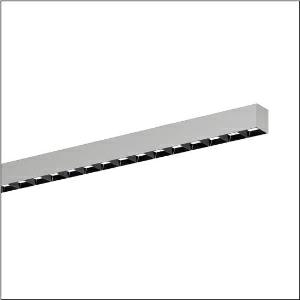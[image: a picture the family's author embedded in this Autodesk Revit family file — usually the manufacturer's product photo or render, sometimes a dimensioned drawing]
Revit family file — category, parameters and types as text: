
# Revit family: silica_r__21_51mx21dc3asb_b009
name_source: partatom
category: Lighting Fixtures
units: mm (PartAtom-declared; Revit-internal decimal feet)

## family parameters
Cut with Voids When Loaded = No
Host = Face
Light Source = No
Part Type = Normal
Room Calculation Point = No
Round Connector Dimension = Use Diameter
Shared = No

## types (1)
- --- (1 x LED, 10800 lm, 69.3 W, 3000K)
    Apparent Load = 69 VA
    CIE Flux Codes = 87 99 100 100 100
    Color Rendering = 80
    Color Temperature = 3000K
    Default Elevation = 1800 mm
    Description = Silica® 21, office luminaire, primary light control with darklight reflector, of PMMA, black, CAT 2 (L<= 3000cd/m²), light emission: direct distribution, primary light characteristic: symmetric, installation type: surface-mounted, LED, rated luminous flux: 10.800lm, luminous efficacy: 156lm/W, light colour: 830, colour temperature: 3000K, with terminal, 3+2-pole, max. 2.5mm², mains connection: 220..240V, AC, 50/60Hz, luminaire housing, of aluminium, metallic grey (RAL 9006), length: 3.004mm, width: 53mm, height: 53mm, protection rating (complete): IP20, insulation class (complete): insulation class I (protective earthing), certification: CE, permissible operating ambient temperature: 0..+35°C, standard: EN 50419, packaging unit: 1 piece
    Height = 0 mm  [stored 0 ft]
    Lamp = 1 x LED
    Lamp Light Flux = 10800 lm
    Lamp Power = 69.3 W
    Lamp count = 1
    Length = 3004 mm
    Luminous efficacy = 156 lm/W
    Manufacturer = Siteco
    ModVariant = No
    Model = 51MX21DC3ASB
    Mounting Place = Ceiling
    Mounting Type = Recessed
    Number of Poles = 1
    OnlyDefault = Yes
    Power Factor = 1
    Product Name = Silica® 21
    Product group = office luminaire | ceiling recessed
    ProductGroupID = 400
    Protection Class = Protection class I
    Protection Degree = IP 20
    RLX_Detail_Level = 1
    RLX_Emergency_Light_Flux = 0 lm
    RLX_Emergency_Type = 0
    RLX_Emergency_Type_DB = No
    RlxData = <blob elided: 63573 chars, md5=67ed1f3a>
    Socket = socket
    Standby Power = 0 W
    System Light Flux = 10800 lm
    System Power = 69 W
    Type Comments = factory setting: luminous flux: 100 % | dim-lin: 254 | 393 mA
    Type Image = l_1335929.jpg
    URL = http://relux.com
    VarID = @adj_093083
    Voltage = 0 V
    Weight = 0.00 kg
    Width = 53 mm

note: [stored X ft] marks values corroborated as IEEE doubles in the binary element streams (Revit-internal decimal feet)

## geometry (parser evidence)
native form markers: Blend x4, Sweep x9
no freeform markers — native parametric forms only
